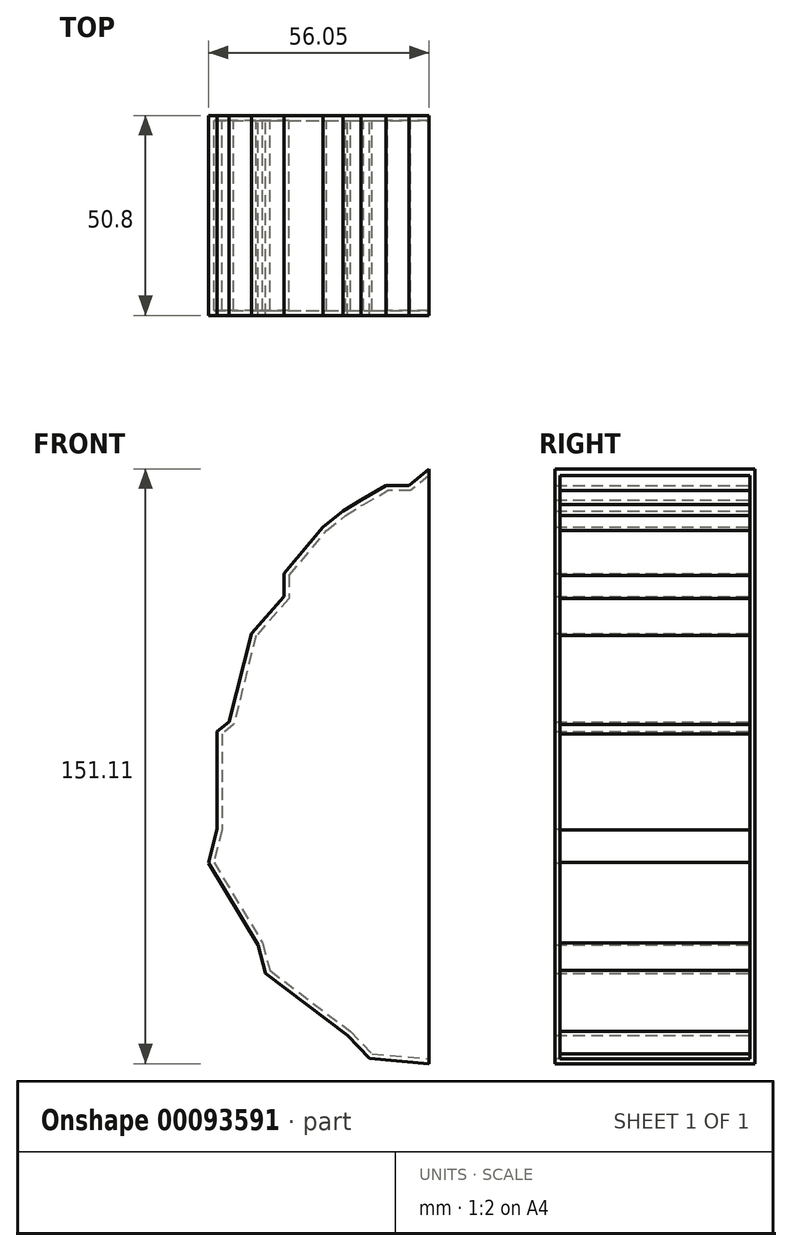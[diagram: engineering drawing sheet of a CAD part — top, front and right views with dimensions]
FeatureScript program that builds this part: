
annotation { "Feature Type Name" : "Feature", "Feature Type Description" : "" }
export const myFeature = defineFeature(function(context is Context, id is Id, definition is map)
    precondition{}
    {
        {
            var Q0;
            Q0=qCreatedBy(makeId("Front.planeOp"),FACE);
            var sketch = newSketch(context, id + "F0", { "sketchPlane" : qUnion([Q0])});
            skLineSegment(sketch, "E0", {"start": v(0, 75.7) * mm, "end": v(0, -75.42) * mm});
            skLineSegment(sketch, "E1", {"start": v(0, 75.7) * mm, "end": v(-5.13, 71.43) * mm});
            skLineSegment(sketch, "E2", {"start": v(-5.13, 71.43) * mm, "end": v(-10.93, 71.43) * mm});
            skLineSegment(sketch, "E3", {"start": v(-36.8, 49.13) * mm, "end": v(-36.8, 43.3) * mm});
            skLineSegment(sketch, "E4", {"start": v(-36.8, 43.3) * mm, "end": v(-45.09, 33.93) * mm});
            skLineSegment(sketch, "E5", {"start": v(-45.09, 33.93) * mm, "end": v(-50.8, 11.43) * mm});
            skLineSegment(sketch, "E6", {"start": v(-50.8, 11.43) * mm, "end": v(-53.84, 9.02) * mm});
            skLineSegment(sketch, "E7", {"start": v(-53.84, 9.02) * mm, "end": v(-53.84, -15.83) * mm});
            skLineSegment(sketch, "E8", {"start": v(-53.84, -15.83) * mm, "end": v(-56.05, -24.45) * mm});
            skLineSegment(sketch, "E9", {"start": v(-56.05, -24.45) * mm, "end": v(-43.45, -45.24) * mm});
            skLineSegment(sketch, "E10", {"start": v(-43.45, -45.24) * mm, "end": v(-41.56, -52.53) * mm});
            skLineSegment(sketch, "E11", {"start": v(-41.56, -52.53) * mm, "end": v(-20.79, -68.18) * mm});
            skLineSegment(sketch, "E12", {"start": v(-20.79, -68.18) * mm, "end": v(-15.12, -74.12) * mm});
            skLineSegment(sketch, "E13", {"start": v(-15.12, -74.12) * mm, "end": v(0, -75.42) * mm});
            skLineSegment(sketch, "E14", {"start": v(-21.9, 64.94) * mm, "end": v(-17.3, 67.8) * mm});
            skLineSegment(sketch, "E15", {"start": v(-17.3, 67.8) * mm, "end": v(-10.93, 71.43) * mm});
            skLineSegment(sketch, "E16", {"start": v(-26.9, 60.93) * mm, "end": v(-21.9, 64.94) * mm});
            skLineSegment(sketch, "E17", {"start": v(-36.8, 49.13) * mm, "end": v(-26.9, 60.93) * mm});
            skSolve(sketch);
        }
        {
            var Q0;
            Q0 = qSketchRegion(id + "F0", true);
            extrude(context, id + "F1", {"entities" : qUnion([Q0]), "depth" : 50.8 * mm});
        }
        {
            var Q0;
            Q0=makeQuery(id+"F1.opExtrude","SWEPT_FACE",FACE,{"disambiguationData":[OSD([sQuery(id+"F0.wireOp",EDGE,"E0")])]});
            shell(context, id + "F2", {"entities" : qUnion([Q0]), "thickness" : 1.27 * mm});
        }
    });
